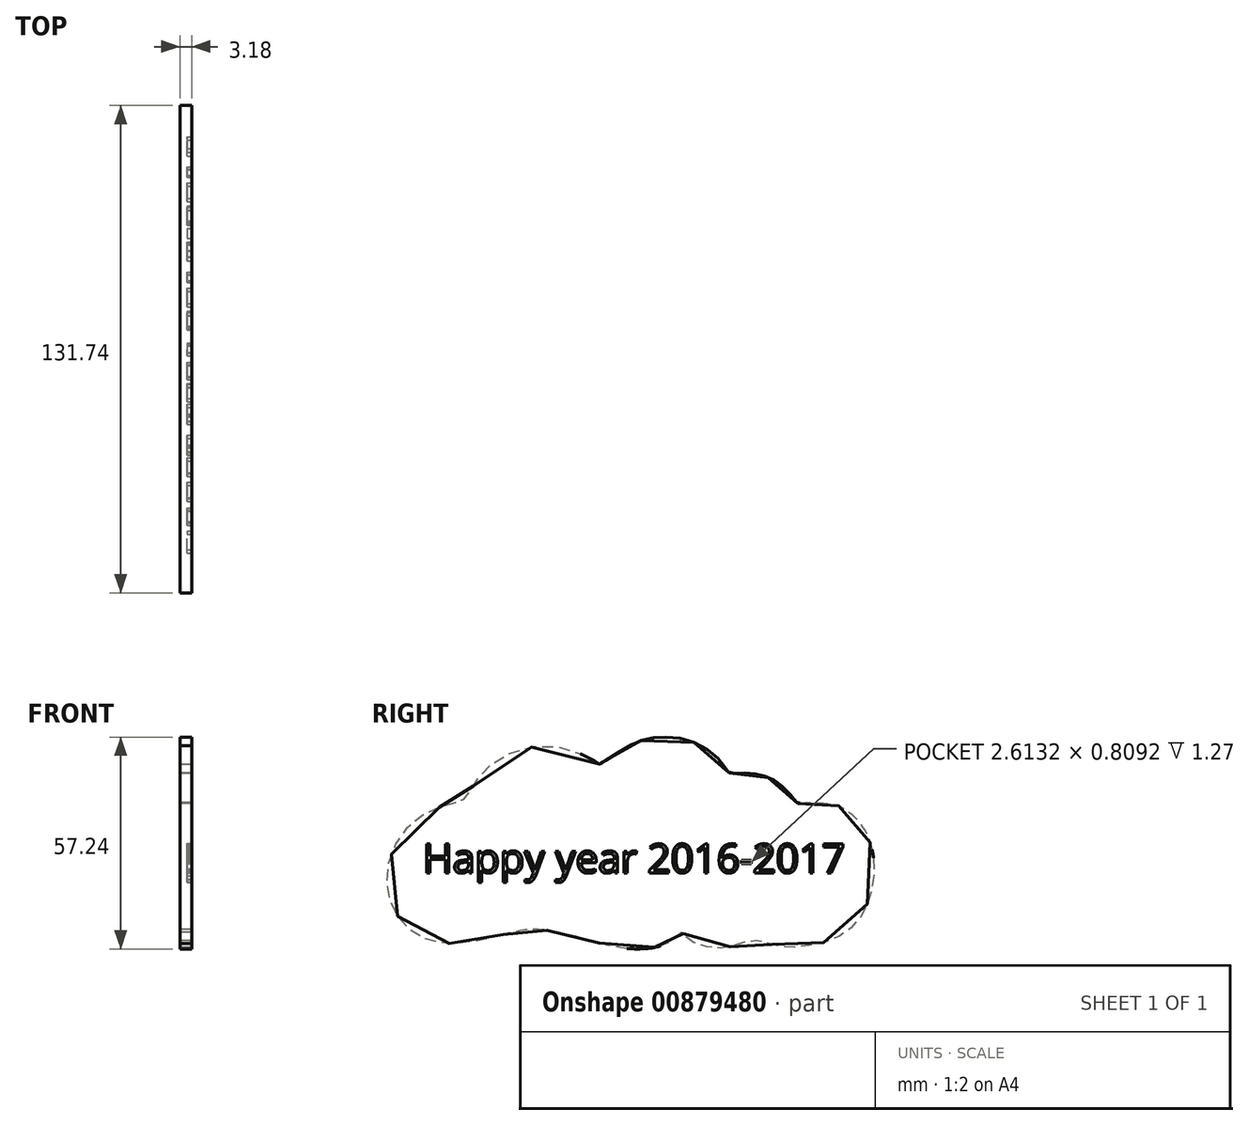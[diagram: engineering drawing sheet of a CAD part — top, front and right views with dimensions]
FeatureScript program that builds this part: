
annotation { "Feature Type Name" : "Feature", "Feature Type Description" : "" }
export const myFeature = defineFeature(function(context is Context, id is Id, definition is map)
    precondition{}
    {
        {
            var Q0;
            Q0=qCreatedBy(makeId("Right.planeOp"),FACE);
            var sketch = newSketch(context, id + "F0", { "sketchPlane" : qUnion([Q0])});
            skFitSpline(sketch, "E0", {"points": [v(-33.71, -20.96) * mm, v(-42.15, -22.85) * mm, v(-54, -22.39) * mm, v(-62.85, -15) * mm, v(-64.82, -2.45) * mm, v(-56.45, 10.84) * mm, v(-45.87, 15.02) * mm, v(-43.55, 16.44) * mm, v(-38.07, 24.14) * mm, v(-18.5, 29.75) * mm, v(-7.57, 25.06) * mm, v(-7.55, 25.06) * mm, v(0, 29.85) * mm, v(7.48, 32.29) * mm, v(18.1, 30.9) * mm, v(26, 24.69) * mm, v(27.5, 22.78) * mm, v(31.6, 22.78) * mm, v(37.42, 21.69) * mm, v(42.25, 18.63) * mm, v(45.87, 14.6) * mm, v(46.27, 14.6) * mm, v(52.7, 14.6) * mm, v(58.34, 13.18) * mm, v(63.75, 7.7) * mm, v(66.56, -2.4) * mm, v(63.43, -15.33) * mm, v(54.88, -22.42) * mm, v(42.8, -24.3) * mm, v(38.3, -23.37) * mm, v(33.38, -22.63) * mm, v(25.26, -24.6) * mm, v(16.1, -22) * mm, v(14.44, -20.34) * mm, v(12.58, -22) * mm, v(7.77, -24.3) * mm, v(-1.82, -24.5) * mm, v(-12.87, -21.8) * mm, v(-21.42, -19.92) * mm, v(-26, -19.5) * mm, v(-33.71, -20.96) * mm]});
            skSolve(sketch);
        }
        {
            var Q0;
            Q0=qSketchRegion(id+"F0",true);
            extrude(context, id + "F1", {"entities" : qUnion([Q0]), "depth" : 3.17 * mm, "offsetDistance" : 25.4 * mm});
        }
        {
            var Q0;
            Q0=makeQuery(id+"F1.opExtrude","CAP_FACE",FACE,{"disambiguationData":[OSD([sQuery(id+"F0.wireOp",EDGE,"E0")])],"isStart":false});
            var sketch = newSketch(context, id + "F2", { "sketchPlane" : qUnion([Q0])});
            skText(sketch, "E1", { "text": "Happy year 2016-2017", "fontName": "OpenSans-Regular.ttf"});
            const initialGuessF2  = {"E1": [-0.05543, -0.00425, 1, 0, 0.00785]};
            skSetInitialGuess(sketch, initialGuessF2);
            skSolve(sketch);
        }
        {
            var Q0;
            Q0 = qSketchRegion(id + "F2", true);
            extrude(context, id + "F3", {"entities" : qUnion([Q0]), "operationType" : NewBodyOperationType.REMOVE, "oppositeDirection" : true, "depth" : 1.27 * mm, "offsetDistance" : 25.4 * mm});
        }
    });
